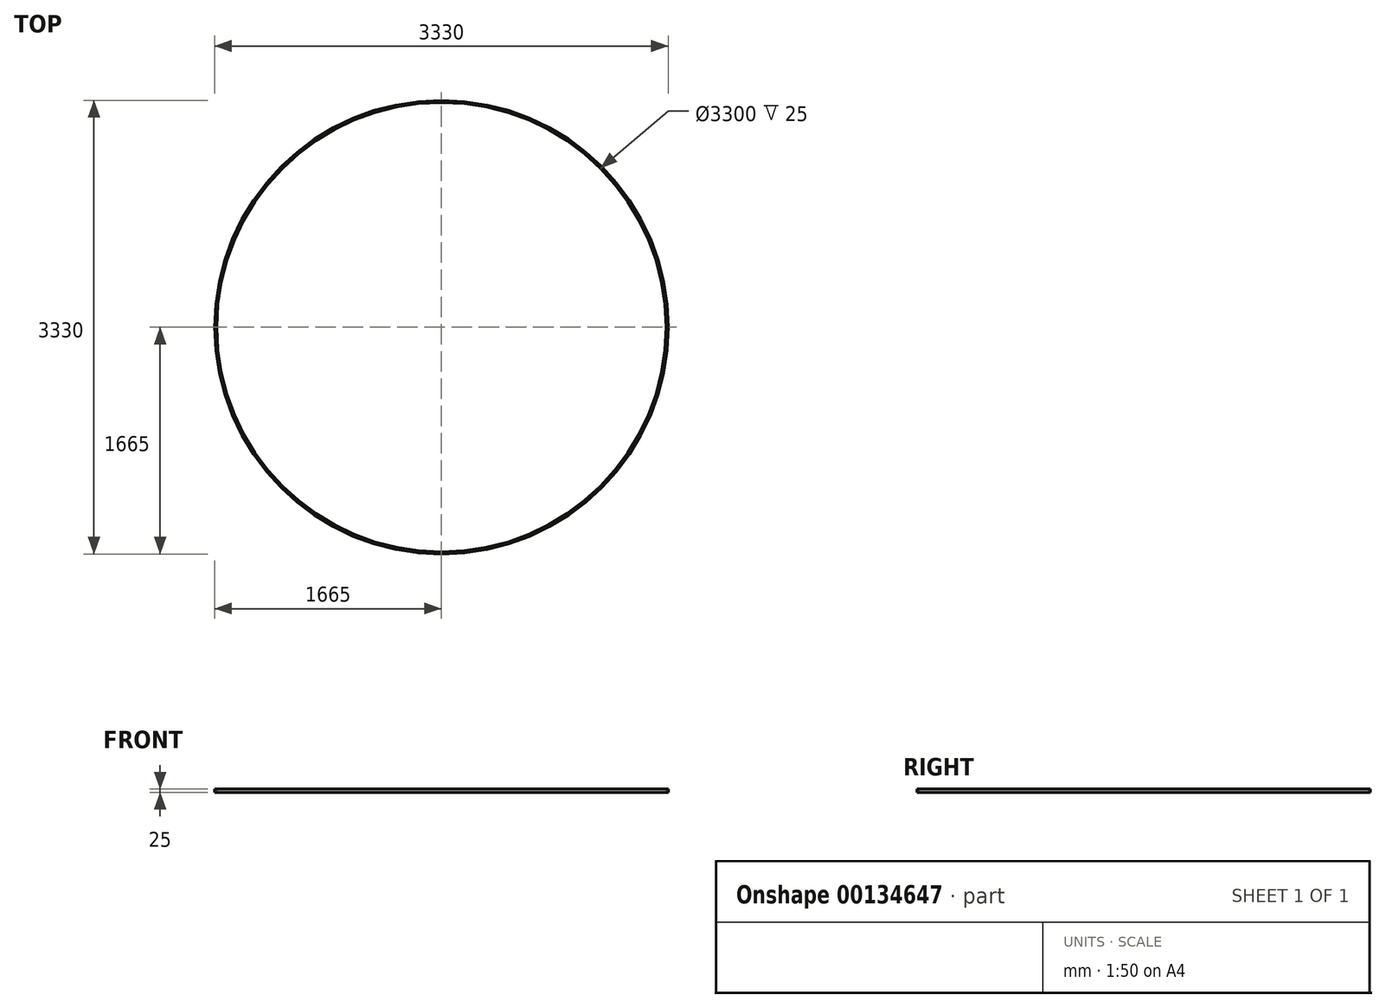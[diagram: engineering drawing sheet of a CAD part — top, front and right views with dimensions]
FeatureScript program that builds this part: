
annotation { "Feature Type Name" : "Feature", "Feature Type Description" : "" }
export const myFeature = defineFeature(function(context is Context, id is Id, definition is map)
    precondition{}
    {
        {
            var Q0;
            Q0=qCreatedBy(makeId("Top.planeOp"),FACE);
            var sketch = newSketch(context, id + "F0", { "sketchPlane" : qUnion([Q0])});
            skCircle(sketch, "E0", {"center": v(0, 0) * mm, "radius": 1665 * mm});
            skCircle(sketch, "E1", {"center": v(0, 0) * mm, "radius": 1650 * mm});
            skSolve(sketch);
        }
        {
            var Q0;
            Q0=makeQuery(id+"F0.imprint","IMPRINT",FACE,{"disambiguationData":[TD([[makeQuery(id+"F0.imprint","IMPRINT",EDGE,{"derivedFrom":sQuery(id+"F0.wireOp",EDGE,"E0")}),1.0]])]});
            extrude(context, id + "F1", {"entities" : qUnion([Q0]), "depth" : 25 * mm});
        }
    });
